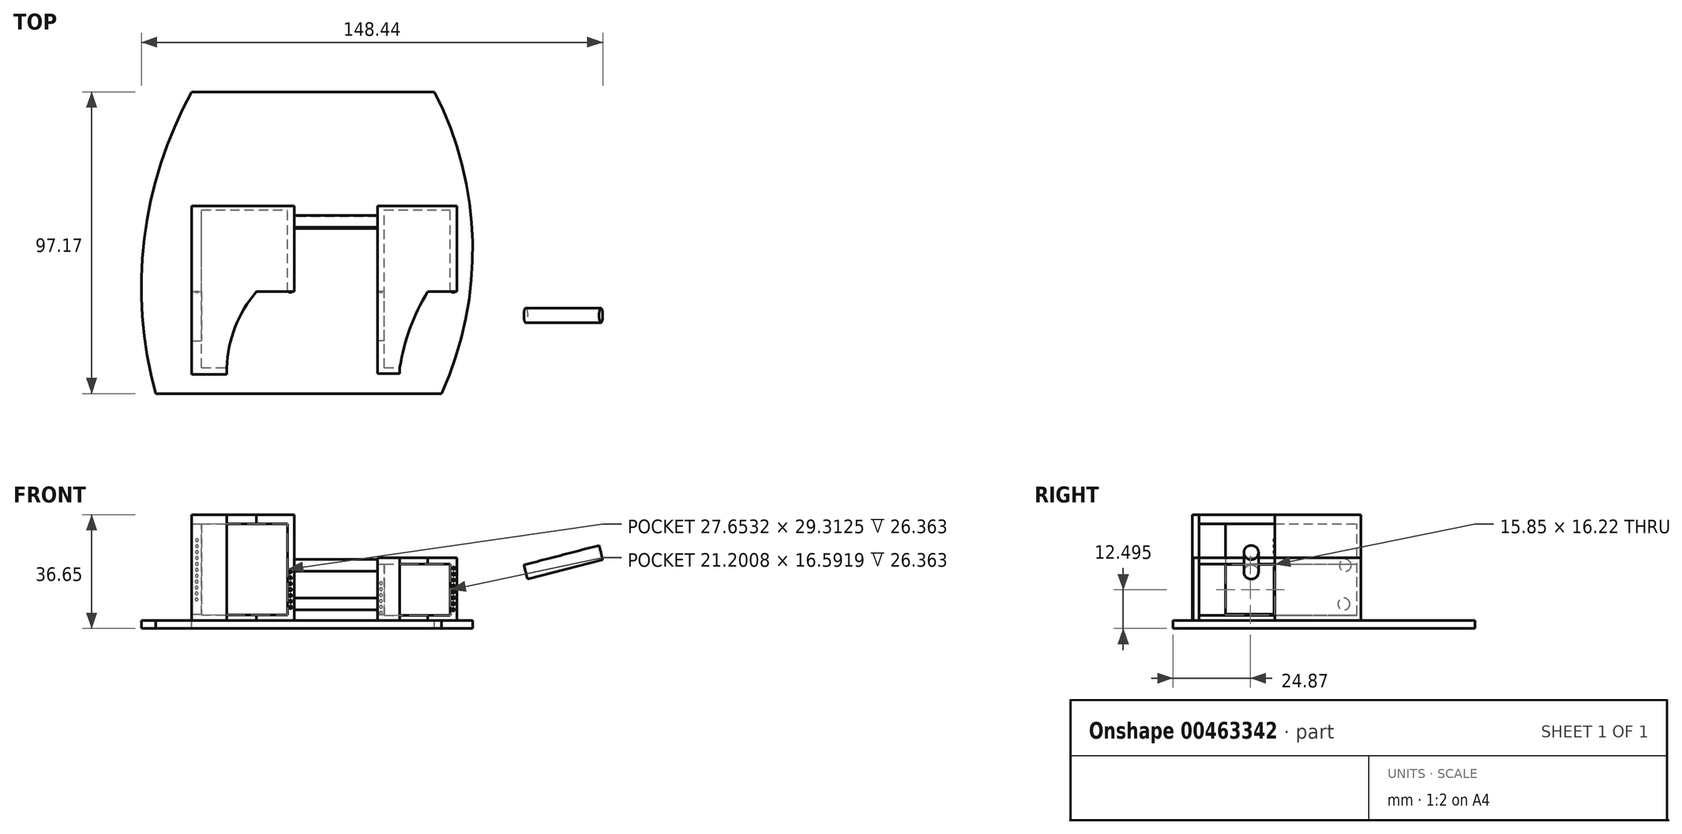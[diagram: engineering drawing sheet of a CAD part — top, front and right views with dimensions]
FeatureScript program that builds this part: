
annotation { "Feature Type Name" : "Feature", "Feature Type Description" : "" }
export const myFeature = defineFeature(function(context is Context, id is Id, definition is map)
    precondition{}
    {
        {
            var Q0;
            Q0=qCreatedBy(makeId("Front.planeOp"),FACE);
            var sketch = newSketch(context, id + "F0", { "sketchPlane" : qUnion([Q0])});
            skLineSegment(sketch, "E0.bottom", {"start": v(-7.56, 0) * mm, "end": v(-40.56, 0) * mm});
            skLineSegment(sketch, "E0.top", {"start": v(-7.56, 34.1) * mm, "end": v(-40.56, 34.1) * mm});
            skLineSegment(sketch, "E0.left", {"start": v(-7.56, 0) * mm, "end": v(-7.56, 34.1) * mm});
            skLineSegment(sketch, "E0.right", {"start": v(-40.56, 0) * mm, "end": v(-40.56, 34.1) * mm});
            skLineSegment(sketch, "E1.bottom", {"start": v(19.17, 0) * mm, "end": v(44.8, 0) * mm});
            skLineSegment(sketch, "E1.top", {"start": v(19.17, 20.28) * mm, "end": v(44.8, 20.28) * mm});
            skLineSegment(sketch, "E1.left", {"start": v(19.17, 0) * mm, "end": v(19.17, 20.28) * mm});
            skLineSegment(sketch, "E1.right", {"start": v(44.8, 0) * mm, "end": v(44.8, 20.28) * mm});
            skLineSegment(sketch, "E2.bottom", {"start": v(-37.42, 1.84) * mm, "end": v(-9.77, 1.84) * mm});
            skLineSegment(sketch, "E2.top", {"start": v(-37.42, 31.16) * mm, "end": v(-9.77, 31.16) * mm});
            skLineSegment(sketch, "E2.left", {"start": v(-37.42, 1.84) * mm, "end": v(-37.42, 31.16) * mm});
            skLineSegment(sketch, "E2.right", {"start": v(-9.77, 1.84) * mm, "end": v(-9.77, 31.16) * mm});
            skLineSegment(sketch, "E3.bottom", {"start": v(21.39, 1.66) * mm, "end": v(42.59, 1.66) * mm});
            skLineSegment(sketch, "E3.top", {"start": v(21.39, 18.25) * mm, "end": v(42.59, 18.25) * mm});
            skLineSegment(sketch, "E3.left", {"start": v(21.39, 1.66) * mm, "end": v(21.39, 18.25) * mm});
            skLineSegment(sketch, "E3.right", {"start": v(42.59, 1.66) * mm, "end": v(42.59, 18.25) * mm});
            skSolve(sketch);
        }
        {
            var Q0;
            Q0=makeQuery(id+"F0.imprint","IMPRINT",FACE,{"disambiguationData":[TD([[makeQuery(id+"F0.imprint","IMPRINT",EDGE,{"derivedFrom":sQuery(id+"F0.wireOp",EDGE,"E0.bottom")}),-1.0]])]});
            var Q1;
            Q1=makeQuery(id+"F0.imprint","IMPRINT",FACE,{"disambiguationData":[TD([[makeQuery(id+"F0.imprint","IMPRINT",EDGE,{"derivedFrom":sQuery(id+"F0.wireOp",EDGE,"E1.bottom")}),1.0]])]});
            extrude(context, id + "F1", {"entities" : qUnion([Q0, Q1]), "depth" : 50.8 * mm});
        }
        {
            var Q0;
            Q0=qCreatedBy(makeId("Right.planeOp"),FACE);
            var sketch = newSketch(context, id + "F2", { "sketchPlane" : qUnion([Q0])});
            skCircle(sketch, "E4", {"center": v(-3.7, 17.8) * mm, "radius": 1.9 * mm});
            skCircle(sketch, "E5", {"center": v(-4.15, 5.36) * mm, "radius": 1.9 * mm});
            skSolve(sketch);
        }
        {
            var Q0;
            Q0 = qSketchRegion(id + "F2", true);
            extrude(context, id + "F3", {"entities" : qUnion([Q0]), "endBound" : BoundingType.UP_TO_NEXT, "depth" : 25.4 * mm, "hasSecondDirection" : true, "secondDirectionBound" : SecondDirectionBoundingType.UP_TO_NEXT, "secondDirectionOppositeDirection" : true, "secondDirectionDepth" : 25.4 * mm});
        }
        {
            var Q0;
            Q0=qCreatedBy(makeId("Top.planeOp"),FACE);
            var sketch = newSketch(context, id + "F4", { "sketchPlane" : qUnion([Q0])});
            skLineSegment(sketch, "E6", {"start": v(-19.73, -26.36) * mm, "end": v(-2.03, -26.36) * mm});
            skLineSegment(sketch, "E7", {"start": v(-2.03, -26.36) * mm, "end": v(-2.03, -63.42) * mm});
            skLineSegment(sketch, "E8", {"start": v(-2.03, -63.42) * mm, "end": v(-27.65, -63.42) * mm});
            skArc(sketch, "E9", {"start": v(-19.73, -26.36) * mm, "mid": v(-28.47, -43.87) * mm, "end": v(-27.65, -63.42) * mm});
            skLineSegment(sketch, "E10", {"start": v(35.37, -26.36) * mm, "end": v(51.44, -26.36) * mm});
            skPoint(sketch, "E10.startSnap0", {"position": v(-10.88, -26.36) * mm});
            skLineSegment(sketch, "E11", {"start": v(51.44, -26.36) * mm, "end": v(51.44, -63.05) * mm});
            skLineSegment(sketch, "E12", {"start": v(51.44, -63.05) * mm, "end": v(25.63, -63.05) * mm});
            skArc(sketch, "E13", {"start": v(35.37, -26.36) * mm, "mid": v(27.8, -43.99) * mm, "end": v(25.63, -63.05) * mm});
            skSolve(sketch);
        }
        {
            var Q0;
            Q0=makeQuery(id+"F4.imprint","IMPRINT",FACE,{"disambiguationData":[TD([[makeQuery(id+"F4.imprint","IMPRINT",EDGE,{"derivedFrom":sQuery(id+"F4.wireOp",EDGE,"E10")}),-1.0]])]});
            var Q1;
            Q1=makeQuery(id+"F4.imprint","IMPRINT",FACE,{"disambiguationData":[TD([[makeQuery(id+"F4.imprint","IMPRINT",EDGE,{"derivedFrom":sQuery(id+"F4.wireOp",EDGE,"E6")}),-1.0]])]});
            extrude(context, id + "F5", {"entities" : qUnion([Q0, Q1]), "operationType" : NewBodyOperationType.REMOVE, "depth" : 101.6 * mm, "hasSecondDirection" : true, "secondDirectionOppositeDirection" : true, "secondDirectionDepth" : 25.4 * mm});
        }
        {
            var Q0;
            Q0=qCreatedBy(makeId("Right.planeOp"),FACE);
            var sketch = newSketch(context, id + "F6", { "sketchPlane" : qUnion([Q0])});
            skLineSegment(sketch, "E14.bottom", {"start": v(-42.22, 18.07) * mm, "end": v(-26.36, 18.07) * mm});
            skLineSegment(sketch, "E14.top", {"start": v(-42.22, 1.84) * mm, "end": v(-26.36, 1.84) * mm});
            skLineSegment(sketch, "E14.left", {"start": v(-42.22, 18.07) * mm, "end": v(-42.22, 1.84) * mm});
            skLineSegment(sketch, "E14.right", {"start": v(-26.36, 18.07) * mm, "end": v(-26.36, 1.84) * mm});
            skSolve(sketch);
        }
        {
            var Q0;
            Q0 = qSketchRegion(id + "F6", true);
            extrude(context, id + "F7", {"entities" : qUnion([Q0]), "operationType" : NewBodyOperationType.REMOVE, "depth" : 101.6 * mm});
        }
        {
            var Q0;
            Q0=qCreatedBy(makeId("Right.planeOp"),FACE);
            var sketch = newSketch(context, id + "F8", { "sketchPlane" : qUnion([Q0])});
            skLineSegment(sketch, "E15.bottom", {"start": v(-42.22, 2.03) * mm, "end": v(-26.36, 2.03) * mm});
            skLineSegment(sketch, "E15.top", {"start": v(-42.22, 31.16) * mm, "end": v(-26.36, 31.16) * mm});
            skLineSegment(sketch, "E15.left", {"start": v(-42.22, 2.03) * mm, "end": v(-42.22, 31.16) * mm});
            skLineSegment(sketch, "E15.right", {"start": v(-26.36, 2.03) * mm, "end": v(-26.36, 31.16) * mm});
            skSolve(sketch);
        }
        {
            var Q0;
            Q0 = qSketchRegion(id + "F8", true);
            extrude(context, id + "F9", {"entities" : qUnion([Q0]), "operationType" : NewBodyOperationType.REMOVE, "oppositeDirection" : true, "depth" : 76.2 * mm});
        }
        {
            var Q0;
            Q0=makeQuery(id+"F5.boolean.opBoolean","COPY",FACE,{"derivedFrom":makeQuery(id+"F5.opExtrude","SWEPT_FACE",FACE,{"disambiguationData":[OSD([sQuery(id+"F4.wireOp",EDGE,"E6")])]})});
            var sketch = newSketch(context, id + "F10", { "sketchPlane" : qUnion([Q0])});
            skCircle(sketch, "E16", {"center": v(-8.94, 15.7) * mm, "radius": 0.44 * mm});
            skCircle(sketch, "E17.1.0.0", {"center": v(-8.9, 13.8) * mm, "radius": 0.44 * mm});
            skCircle(sketch, "E17.2.0.0", {"center": v(-8.87, 11.9) * mm, "radius": 0.44 * mm});
            skCircle(sketch, "E17.3.0.0", {"center": v(-8.84, 10) * mm, "radius": 0.44 * mm});
            skCircle(sketch, "E17.4.0.0", {"center": v(-8.8, 8.1) * mm, "radius": 0.44 * mm});
            skCircle(sketch, "E17.5.0.0", {"center": v(-8.77, 6.19) * mm, "radius": 0.44 * mm});
            skCircle(sketch, "E17.6.0.0", {"center": v(-8.74, 4.28) * mm, "radius": 0.44 * mm});
            skLineSegment(sketch, "E17.direction1", {"start": v(-8.94, 15.7) * mm, "end": v(-8.9, 13.8) * mm, "construction": true});
            skSolve(sketch);
        }
        {
            var Q0;
            Q0 = qSketchRegion(id + "F10", true);
            extrude(context, id + "F11", {"entities" : qUnion([Q0]), "depth" : 0.25 * mm});
        }
        {
            var Q0;
            Q0=makeQuery(id+"F9.boolean.opBoolean","COPY",FACE,{"derivedFrom":makeQuery(id+"F9.opExtrude","SWEPT_FACE",FACE,{"disambiguationData":[OSD([sQuery(id+"F8.wireOp",EDGE,"E15.right")])]})});
            var sketch = newSketch(context, id + "F12", { "sketchPlane" : qUnion([Q0])});
            skCircle(sketch, "E18", {"center": v(-38.87, 25.88) * mm, "radius": 0.44 * mm});
            skCircle(sketch, "E19.1.0.0", {"center": v(-38.89, 23.98) * mm, "radius": 0.44 * mm});
            skCircle(sketch, "E19.2.0.0", {"center": v(-38.9, 22.07) * mm, "radius": 0.44 * mm});
            skCircle(sketch, "E19.3.0.0", {"center": v(-38.92, 20.17) * mm, "radius": 0.44 * mm});
            skCircle(sketch, "E19.4.0.0", {"center": v(-38.93, 18.26) * mm, "radius": 0.44 * mm});
            skCircle(sketch, "E19.5.0.0", {"center": v(-38.94, 16.36) * mm, "radius": 0.44 * mm});
            skCircle(sketch, "E19.6.0.0", {"center": v(-38.96, 14.45) * mm, "radius": 0.44 * mm});
            skCircle(sketch, "E19.7.0.0", {"center": v(-38.97, 12.55) * mm, "radius": 0.44 * mm});
            skCircle(sketch, "E19.8.0.0", {"center": v(-38.99, 10.64) * mm, "radius": 0.44 * mm});
            skCircle(sketch, "E19.9.0.0", {"center": v(-39, 8.74) * mm, "radius": 0.44 * mm});
            skLineSegment(sketch, "E19.direction1", {"start": v(-38.87, 25.88) * mm, "end": v(-38.89, 23.98) * mm, "construction": true});
            skCircle(sketch, "E20.0.10.0", {"center": v(-39.02, 6.83) * mm, "radius": 0.44 * mm});
            skSolve(sketch);
        }
        {
            var Q0;
            Q0 = qSketchRegion(id + "F12", true);
            extrude(context, id + "F13", {"entities" : qUnion([Q0]), "depth" : 0.25 * mm});
        }
        {
            var Q0;
            Q0=makeQuery(id+"F7.boolean.opBoolean","COPY",FACE,{"derivedFrom":makeQuery(id+"F7.opExtrude","SWEPT_FACE",FACE,{"disambiguationData":[OSD([sQuery(id+"F6.wireOp",EDGE,"E14.right")])]})});
            var sketch = newSketch(context, id + "F14", { "sketchPlane" : qUnion([Q0])});
            skCircle(sketch, "E21", {"center": v(20.33, 12.05) * mm, "radius": 0.44 * mm});
            skCircle(sketch, "E22.1.0.0", {"center": v(20.33, 10.14) * mm, "radius": 0.44 * mm});
            skCircle(sketch, "E22.2.0.0", {"center": v(20.33, 8.24) * mm, "radius": 0.44 * mm});
            skCircle(sketch, "E22.3.0.0", {"center": v(20.32, 6.33) * mm, "radius": 0.44 * mm});
            skCircle(sketch, "E22.4.0.0", {"center": v(20.32, 4.43) * mm, "radius": 0.44 * mm});
            skCircle(sketch, "E22.5.0.0", {"center": v(20.32, 2.52) * mm, "radius": 0.44 * mm});
            skLineSegment(sketch, "E22.direction1", {"start": v(20.33, 12.05) * mm, "end": v(20.33, 10.14) * mm, "construction": true});
            skSolve(sketch);
        }
        {
            var Q0;
            Q0 = qSketchRegion(id + "F14", true);
            extrude(context, id + "F15", {"entities" : qUnion([Q0]), "depth" : 0.25 * mm});
        }
        {
            var Q0;
            Q0=makeQuery(id+"F5.boolean.opBoolean","COPY",FACE,{"derivedFrom":makeQuery(id+"F5.opExtrude","SWEPT_FACE",FACE,{"disambiguationData":[OSD([sQuery(id+"F4.wireOp",EDGE,"E6")])]})});
            var sketch = newSketch(context, id + "F16", { "sketchPlane" : qUnion([Q0])});
            skCircle(sketch, "E23", {"center": v(43.68, 16.86) * mm, "radius": 0.44 * mm});
            skCircle(sketch, "E24.1.0.0", {"center": v(43.66, 14.96) * mm, "radius": 0.44 * mm});
            skCircle(sketch, "E24.2.0.0", {"center": v(43.65, 13.05) * mm, "radius": 0.44 * mm});
            skCircle(sketch, "E24.3.0.0", {"center": v(43.63, 11.15) * mm, "radius": 0.44 * mm});
            skCircle(sketch, "E24.4.0.0", {"center": v(43.61, 9.24) * mm, "radius": 0.44 * mm});
            skCircle(sketch, "E24.5.0.0", {"center": v(43.6, 7.34) * mm, "radius": 0.44 * mm});
            skCircle(sketch, "E24.6.0.0", {"center": v(43.58, 5.43) * mm, "radius": 0.44 * mm});
            skCircle(sketch, "E24.7.0.0", {"center": v(43.56, 3.53) * mm, "radius": 0.44 * mm});
            skLineSegment(sketch, "E24.direction1", {"start": v(43.68, 16.86) * mm, "end": v(43.66, 14.96) * mm, "construction": true});
            skSolve(sketch);
        }
        {
            var Q0;
            Q0 = qSketchRegion(id + "F16", true);
            extrude(context, id + "F17", {"entities" : qUnion([Q0]), "depth" : 0.25 * mm});
        }
        {
            var Q0;
            Q0=makeQuery(id+"F1.opExtrude","CAP_FACE",FACE,{"disambiguationData":[OSD([sQuery(id+"F0.wireOp",EDGE,"E0.bottom"),sQuery(id+"F0.wireOp",EDGE,"E0.top"),sQuery(id+"F0.wireOp",EDGE,"E0.left"),sQuery(id+"F0.wireOp",EDGE,"E0.right"),sQuery(id+"F0.wireOp",EDGE,"E2.bottom"),sQuery(id+"F0.wireOp",EDGE,"E2.top"),sQuery(id+"F0.wireOp",EDGE,"E2.left"),sQuery(id+"F0.wireOp",EDGE,"E2.right")])],"isStart":false});
            var sketch = newSketch(context, id + "F18", { "sketchPlane" : qUnion([Q0])});
            skLineSegment(sketch, "E25.bottom", {"start": v(-40.56, 34.1) * mm, "end": v(-29.32, 34.1) * mm});
            skLineSegment(sketch, "E25.top", {"start": v(-40.56, 0) * mm, "end": v(-29.32, 0) * mm});
            skLineSegment(sketch, "E25.left", {"start": v(-40.56, 34.1) * mm, "end": v(-40.56, 0) * mm});
            skLineSegment(sketch, "E25.right", {"start": v(-29.32, 34.1) * mm, "end": v(-29.32, 0) * mm});
            skSolve(sketch);
        }
        {
            var Q0;
            Q0 = qSketchRegion(id + "F18", true);
            extrude(context, id + "F19", {"entities" : qUnion([Q0]), "operationType" : NewBodyOperationType.ADD, "depth" : 2.16 * mm});
        }
        {
            var Q0;
            Q0=makeQuery(id+"F1.opExtrude","CAP_FACE",FACE,{"disambiguationData":[OSD([sQuery(id+"F0.wireOp",EDGE,"E1.bottom"),sQuery(id+"F0.wireOp",EDGE,"E1.top"),sQuery(id+"F0.wireOp",EDGE,"E1.left"),sQuery(id+"F0.wireOp",EDGE,"E1.right"),sQuery(id+"F0.wireOp",EDGE,"E3.bottom"),sQuery(id+"F0.wireOp",EDGE,"E3.top"),sQuery(id+"F0.wireOp",EDGE,"E3.left"),sQuery(id+"F0.wireOp",EDGE,"E3.right")])],"isStart":false});
            var sketch = newSketch(context, id + "F20", { "sketchPlane" : qUnion([Q0])});
            skLineSegment(sketch, "E26.bottom", {"start": v(19.17, 20.28) * mm, "end": v(26.37, 20.28) * mm});
            skLineSegment(sketch, "E26.top", {"start": v(19.17, 0) * mm, "end": v(26.37, 0) * mm});
            skLineSegment(sketch, "E26.left", {"start": v(19.17, 20.28) * mm, "end": v(19.17, 0) * mm});
            skLineSegment(sketch, "E26.right", {"start": v(26.37, 20.28) * mm, "end": v(26.37, 0) * mm});
            skSolve(sketch);
        }
        {
            var Q0;
            Q0 = qSketchRegion(id + "F20", true);
            extrude(context, id + "F21", {"entities" : qUnion([Q0]), "operationType" : NewBodyOperationType.ADD, "depth" : 1.9 * mm});
        }
        {
            var Q0;
            Q0=makeQuery(id+"F5.boolean.opBoolean","COPY",FACE,{"derivedFrom":makeQuery(id+"F5.opExtrude","SWEPT_FACE",FACE,{"disambiguationData":[OSD([sQuery(id+"F4.wireOp",EDGE,"E10")])]})});
            cPlane(context, id + "F22", {"entities" : qUnion([Q0]), "cplaneType" : CPlaneType.OFFSET, "offset" : 7.62 * mm, "width" : 152.4 * mm, "height" : 152.4 * mm});
        }
        {
            var Q0;
            Q0=qCreatedBy(id+"F22.planeOp",FACE);
            var sketch = newSketch(context, id + "F23", { "sketchPlane" : qUnion([Q0])});
            skLineSegment(sketch, "E27", {"start": v(66.97, 15.66) * mm, "end": v(91.07, 21.93) * mm});
            skLineSegment(sketch, "E28", {"start": v(91.07, 21.93) * mm, "end": v(90.47, 24.21) * mm});
            skLineSegment(sketch, "E29", {"start": v(90.47, 24.21) * mm, "end": v(66.27, 17.92) * mm});
            skLineSegment(sketch, "E30", {"start": v(66.27, 17.92) * mm, "end": v(66.97, 15.66) * mm});
            skSolve(sketch);
        }
        {
            var Q0;
            Q0=makeQuery(id+"F23.imprint","IMPRINT",FACE,{"disambiguationData":[TD([[makeQuery(id+"F23.imprint","IMPRINT",EDGE,{"derivedFrom":sQuery(id+"F23.wireOp",EDGE,"E27")}),1.0]])]});
            var Q1;
            Q1=sQuery(id+"F23.wireOp",EDGE,"E27");
            revolve(context, id + "F24", {"entities" : qUnion([Q0]), "axis" : qUnion([Q1]), "revolveType" : RevolveType.FULL});
        }
        {
            var Q0;
            Q0=makeQuery(id+"F1.opExtrude","CAP_FACE",FACE,{"disambiguationData":[OSD([sQuery(id+"F0.wireOp",EDGE,"E0.bottom"),sQuery(id+"F0.wireOp",EDGE,"E0.top"),sQuery(id+"F0.wireOp",EDGE,"E0.left"),sQuery(id+"F0.wireOp",EDGE,"E0.right"),sQuery(id+"F0.wireOp",EDGE,"E2.bottom"),sQuery(id+"F0.wireOp",EDGE,"E2.top"),sQuery(id+"F0.wireOp",EDGE,"E2.left"),sQuery(id+"F0.wireOp",EDGE,"E2.right")])],"isStart":true});
            var sketch = newSketch(context, id + "F25", { "sketchPlane" : qUnion([Q0])});
            skLineSegment(sketch, "E31.bottom", {"start": v(7.56, 34.1) * mm, "end": v(40.56, 34.1) * mm});
            skLineSegment(sketch, "E31.top", {"start": v(7.56, 0) * mm, "end": v(40.56, 0) * mm});
            skLineSegment(sketch, "E31.left", {"start": v(7.56, 34.1) * mm, "end": v(7.56, 0) * mm});
            skLineSegment(sketch, "E31.right", {"start": v(40.56, 34.1) * mm, "end": v(40.56, 0) * mm});
            skSolve(sketch);
        }
        {
            var Q0;
            Q0 = qSketchRegion(id + "F25", true);
            extrude(context, id + "F26", {"entities" : qUnion([Q0]), "operationType" : NewBodyOperationType.ADD, "depth" : 1.27 * mm});
        }
        {
            var Q0;
            Q0=makeQuery(id+"F1.opExtrude","CAP_FACE",FACE,{"disambiguationData":[OSD([sQuery(id+"F0.wireOp",EDGE,"E1.bottom"),sQuery(id+"F0.wireOp",EDGE,"E1.top"),sQuery(id+"F0.wireOp",EDGE,"E1.left"),sQuery(id+"F0.wireOp",EDGE,"E1.right"),sQuery(id+"F0.wireOp",EDGE,"E3.bottom"),sQuery(id+"F0.wireOp",EDGE,"E3.top"),sQuery(id+"F0.wireOp",EDGE,"E3.left"),sQuery(id+"F0.wireOp",EDGE,"E3.right")])],"isStart":true});
            var sketch = newSketch(context, id + "F27", { "sketchPlane" : qUnion([Q0])});
            skLineSegment(sketch, "E32.bottom", {"start": v(-44.8, 20.28) * mm, "end": v(-19.17, 20.28) * mm});
            skLineSegment(sketch, "E32.top", {"start": v(-44.8, 0) * mm, "end": v(-19.17, 0) * mm});
            skLineSegment(sketch, "E32.left", {"start": v(-44.8, 20.28) * mm, "end": v(-44.8, 0) * mm});
            skLineSegment(sketch, "E32.right", {"start": v(-19.17, 20.28) * mm, "end": v(-19.17, 0) * mm});
            skSolve(sketch);
        }
        {
            var Q0;
            Q0 = qSketchRegion(id + "F27", true);
            extrude(context, id + "F28", {"entities" : qUnion([Q0]), "operationType" : NewBodyOperationType.ADD, "depth" : 1.27 * mm});
        }
        {
            var Q0;
            Q0=makeQuery(id+"F26.boolean.opBoolean","MERGE",FACE,{"derivedFrom":[makeQuery(id+"F19.boolean.opBoolean","MERGE",FACE,{"derivedFrom":[makeQuery(id+"F1.opExtrude","SWEPT_FACE",FACE,{"disambiguationData":[OSD([sQuery(id+"F0.wireOp",EDGE,"E0.bottom")])]}),makeQuery(id+"F19.opExtrude","SWEPT_FACE",FACE,{"disambiguationData":[OSD([sQuery(id+"F18.wireOp",EDGE,"E25.top")])]})]}),makeQuery(id+"F26.opExtrude","SWEPT_FACE",FACE,{"disambiguationData":[OSD([sQuery(id+"F25.wireOp",EDGE,"E31.top")])]})]});
            var sketch = newSketch(context, id + "F29", { "sketchPlane" : qUnion([Q0])});
            skLineSegment(sketch, "E33", {"start": v(39.82, 59.16) * mm, "end": v(-52.22, 59.16) * mm});
            skLineSegment(sketch, "E34", {"start": v(-40.56, -38) * mm, "end": v(37.54, -38) * mm});
            skArc(sketch, "E35", {"start": v(-52.22, 59.16) * mm, "mid": v(-55.85, 9.44) * mm, "end": v(-40.56, -38) * mm});
            skArc(sketch, "E36", {"start": v(37.54, -38) * mm, "mid": v(49.77, 10.31) * mm, "end": v(39.82, 59.16) * mm});
            skSolve(sketch);
        }
        {
            var Q0;
            Q0 = qSketchRegion(id + "F29", true);
            extrude(context, id + "F30", {"entities" : qUnion([Q0]), "depth" : 2.54 * mm});
        }
    });
